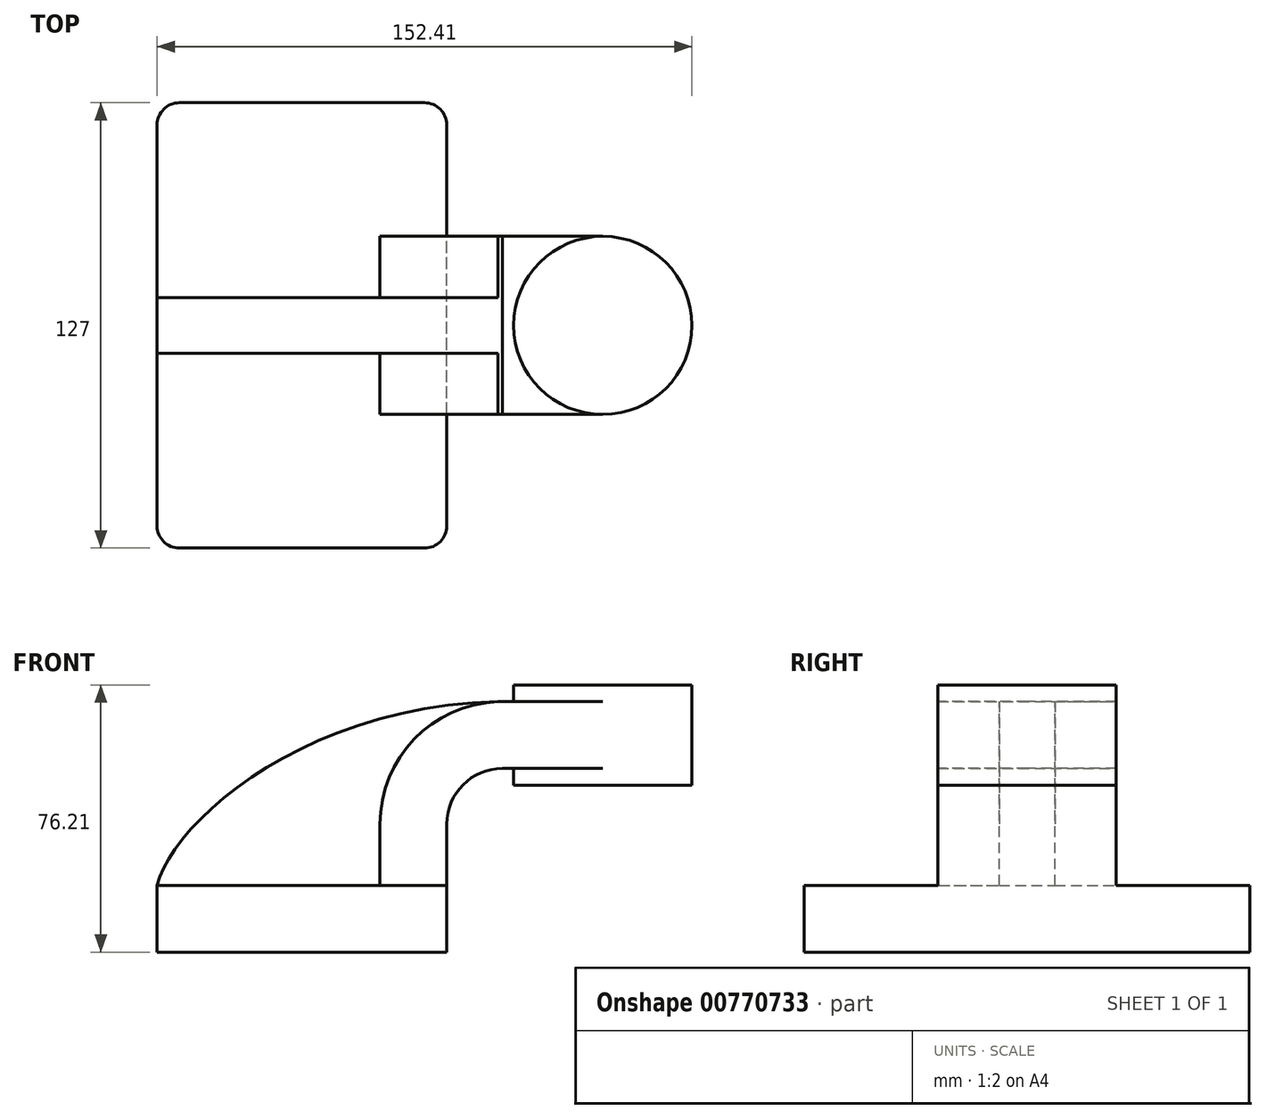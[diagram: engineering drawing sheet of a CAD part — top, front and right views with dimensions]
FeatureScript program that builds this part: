
annotation { "Feature Type Name" : "Feature", "Feature Type Description" : "" }
export const myFeature = defineFeature(function(context is Context, id is Id, definition is map)
    precondition{}
    {
        {
            var Q0;
            Q0=qCreatedBy(makeId("Front.planeOp"),FACE);
            var sketch = newSketch(context, id + "F0", { "sketchPlane" : qUnion([Q0])});
            skLineSegment(sketch, "E0.bottom", {"start": v(41.27, 9.53) * mm, "end": v(-41.27, 9.53) * mm});
            skLineSegment(sketch, "E0.top", {"start": v(41.28, -9.52) * mm, "end": v(-41.27, -9.52) * mm});
            skLineSegment(sketch, "E0.left", {"start": v(41.28, 9.53) * mm, "end": v(41.28, -9.52) * mm});
            skLineSegment(sketch, "E0.right", {"start": v(-41.27, 9.53) * mm, "end": v(-41.27, -9.52) * mm});
            skPoint(sketch, "E0.middle", {"position": v(0, 0) * mm});
            skLineSegment(sketch, "E1.bottom", {"start": v(60.32, 66.68) * mm, "end": v(111.12, 66.68) * mm});
            skLineSegment(sketch, "E1.top", {"start": v(60.32, 38.1) * mm, "end": v(111.12, 38.1) * mm});
            skLineSegment(sketch, "E1.left", {"start": v(60.32, 66.68) * mm, "end": v(60.32, 38.1) * mm});
            skLineSegment(sketch, "E1.right", {"start": v(111.12, 66.68) * mm, "end": v(111.12, 38.1) * mm});
            skPoint(sketch, "E1.middle", {"position": v(85.72, 52.39) * mm});
            skLineSegment(sketch, "E2", {"start": v(41.27, 9.53) * mm, "end": v(41.27, 26.99) * mm});
            skArc(sketch, "E3", {"start": v(41.27, 26.99) * mm, "mid": v(45.92, 38.21) * mm, "end": v(57.15, 42.86) * mm});
            skLineSegment(sketch, "E4", {"start": v(57.15, 42.86) * mm, "end": v(85.72, 42.86) * mm});
            skLineSegment(sketch, "E5.0", {"start": v(57.15, 61.91) * mm, "end": v(85.72, 61.91) * mm});
            skArc(sketch, "E5.1", {"start": v(22.22, 26.99) * mm, "mid": v(32.45, 51.68) * mm, "end": v(57.15, 61.91) * mm});
            skLineSegment(sketch, "E5.2", {"start": v(22.22, 9.53) * mm, "end": v(22.22, 26.99) * mm});
            skLineSegment(sketch, "E6", {"start": v(85.72, 38.1) * mm, "end": v(85.72, 66.68) * mm});
            skFitSpline(sketch, "E7", {"points": [v(-41.27, 9.53) * mm, v(57.15, 61.91) * mm], "startDerivative": vector(12.8, 52.28) * mm, "endDerivative": vector(171.45, 2.4) * mm});
            skSolve(sketch);
        }
        {
            var Q0;
            Q0=makeQuery(id+"F0.imprint","IMPRINT",FACE,{"disambiguationData":[TD([[makeQuery(id+"F0.imprint","IMPRINT",EDGE,{"derivedFrom":sQuery(id+"F0.wireOp",EDGE,"E0.top")}),-1.0]])]});
            extrude(context, id + "F1", {"entities" : qUnion([Q0]), "endBound" : BoundingType.SYMMETRIC, "depth" : 127 * mm, "offsetDistance" : 25.4 * mm});
        }
        {
            var Q0;
            {var subQ1=sQuery(id+"F0.wireOp",EDGE,"E2");Q0=makeQuery(id+"F0.imprint","IMPRINT",FACE,{"disambiguationData":[TD([[makeQuery(id+"F0.imprint","IMPRINT",EDGE,{"derivedFrom":subQ1}),1.0]])]});}
            var Q1;
            {var subQ0=sQuery(id+"F0.wireOp",EDGE,"E5.0");var subQ1=sQuery(id+"F0.wireOp",EDGE,"E1.left");var subQ2=makeQuery(id+"F0.imprint","INTERSECT",VERTEX,{"derivedFrom":[subQ1,subQ0]});Q1=makeQuery(id+"F0.imprint","IMPRINT",FACE,{"disambiguationData":[TD([[makeQuery(id+"F0.imprint","IMPRINT",EDGE,{"disambiguationData":[TD([[subQ2,-1.0]])],"derivedFrom":subQ1}),1.0]])]});}
            extrude(context, id + "F2", {"entities" : qUnion([Q0, Q1]), "operationType" : NewBodyOperationType.ADD, "endBound" : BoundingType.SYMMETRIC, "depth" : 50.8 * mm, "offsetDistance" : 25.4 * mm});
        }
        {
            var Q0;
            {var subQ3=sQuery(id+"F0.wireOp",EDGE,"E5.2");Q0=makeQuery(id+"F0.imprint","IMPRINT",FACE,{"disambiguationData":[TD([[makeQuery(id+"F0.imprint","IMPRINT",EDGE,{"derivedFrom":subQ3}),1.0]])]});}
            extrude(context, id + "F3", {"entities" : qUnion([Q0]), "operationType" : NewBodyOperationType.ADD, "endBound" : BoundingType.SYMMETRIC, "depth" : 15.88 * mm, "offsetDistance" : 25.4 * mm});
        }
        {
            var Q0;
            {var subQ4=sQuery(id+"F0.wireOp",EDGE,"E1.right");Q0=makeQuery(id+"F0.imprint","IMPRINT",FACE,{"disambiguationData":[TD([[makeQuery(id+"F0.imprint","IMPRINT",EDGE,{"derivedFrom":subQ4}),-1.0]])]});}
            var Q1;
            Q1=sQuery(id+"F0.wireOp",EDGE,"E6");
            revolve(context, id + "F4", {"operationType" : NewBodyOperationType.ADD, "surfaceOperationType" : NewSurfaceOperationType.NEW, "entities" : qUnion([Q0]), "axis" : qUnion([Q1]), "revolveType" : RevolveType.FULL});
        }
        {
            var Q0;
            Q0=makeQuery(id+"F1.opExtrude","CAP_EDGE",EDGE,{"disambiguationData":[OSD([sQuery(id+"F0.wireOp",EDGE,"E0.right")])],"isStart":false});
            var Q1;
            Q1=makeQuery(id+"F1.opExtrude","CAP_EDGE",EDGE,{"disambiguationData":[OSD([sQuery(id+"F0.wireOp",EDGE,"E0.left")])],"isStart":false});
            var Q2;
            Q2=makeQuery(id+"F1.opExtrude","CAP_EDGE",EDGE,{"disambiguationData":[OSD([sQuery(id+"F0.wireOp",EDGE,"E0.left")])],"isStart":true});
            var Q3;
            Q3=makeQuery(id+"F1.opExtrude","CAP_EDGE",EDGE,{"disambiguationData":[OSD([sQuery(id+"F0.wireOp",EDGE,"E0.right")])],"isStart":true});
            fillet(context, id + "F5", {"entities" : qUnion([Q0, Q1, Q2, Q3]), "radius" : 6.35 * mm, "tangentPropagation" : true, "allowEdgeOverflow" : false});
        }
    });
